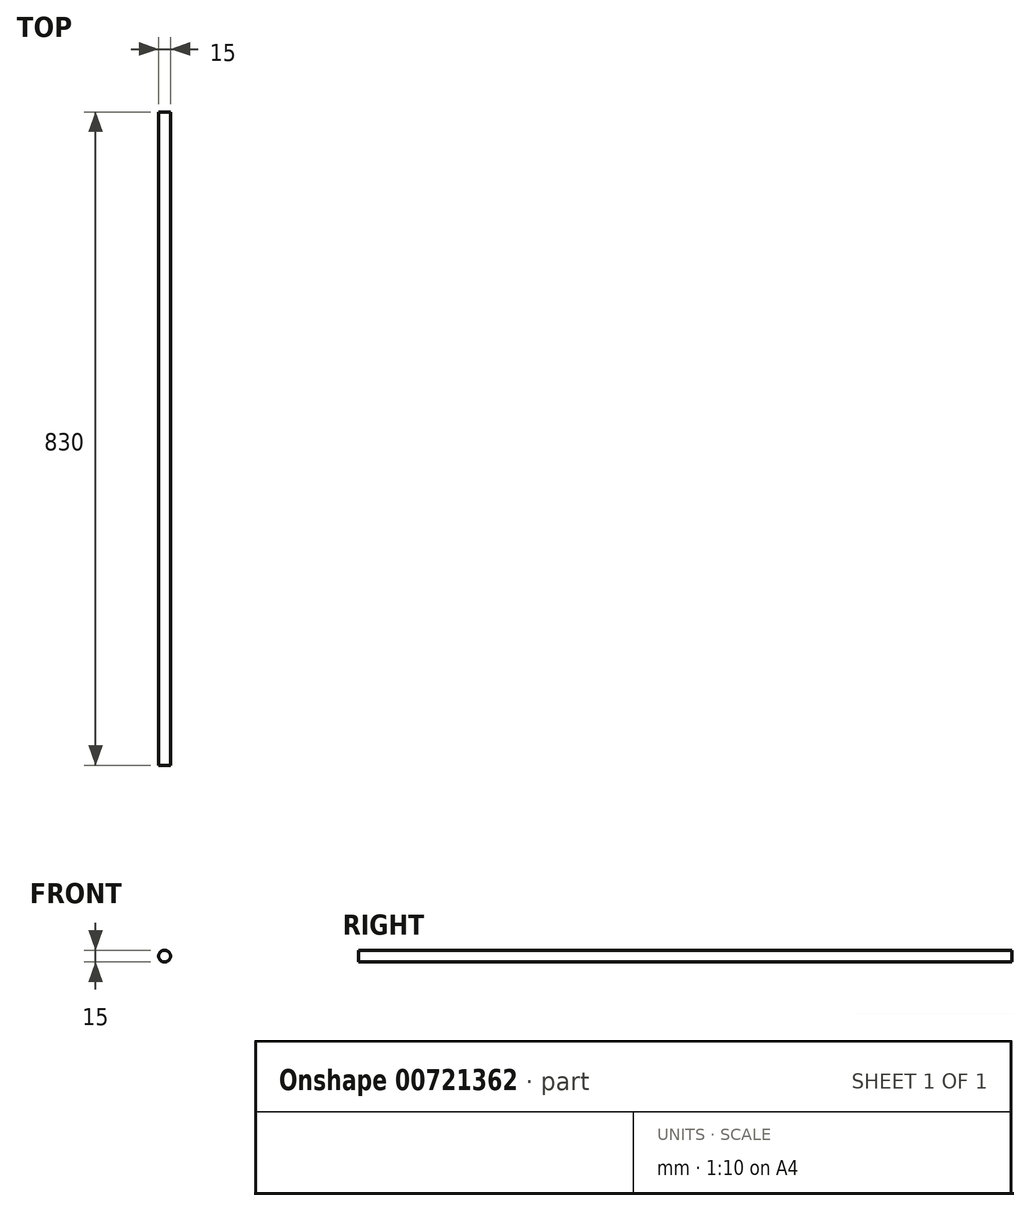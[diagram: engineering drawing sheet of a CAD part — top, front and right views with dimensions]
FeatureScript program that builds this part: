
annotation { "Feature Type Name" : "Feature", "Feature Type Description" : "" }
export const myFeature = defineFeature(function(context is Context, id is Id, definition is map)
    precondition{}
    {
        {
            var Q0;
            Q0=qCreatedBy(makeId("Front.planeOp"),FACE);
            var sketch = newSketch(context, id + "F0", { "sketchPlane" : qUnion([Q0])});
            skCircle(sketch, "E0", {"center": v(0, 0) * mm, "radius": 7.5 * mm});
            skSolve(sketch);
        }
        {
            var Q0;
            Q0=qSketchRegion(id+"F0",true);
            extrude(context, id + "F1", {"entities" : qUnion([Q0]), "endBound" : BoundingType.SYMMETRIC, "depth" : 830 * mm, "offsetDistance" : 25 * mm});
        }
    });
